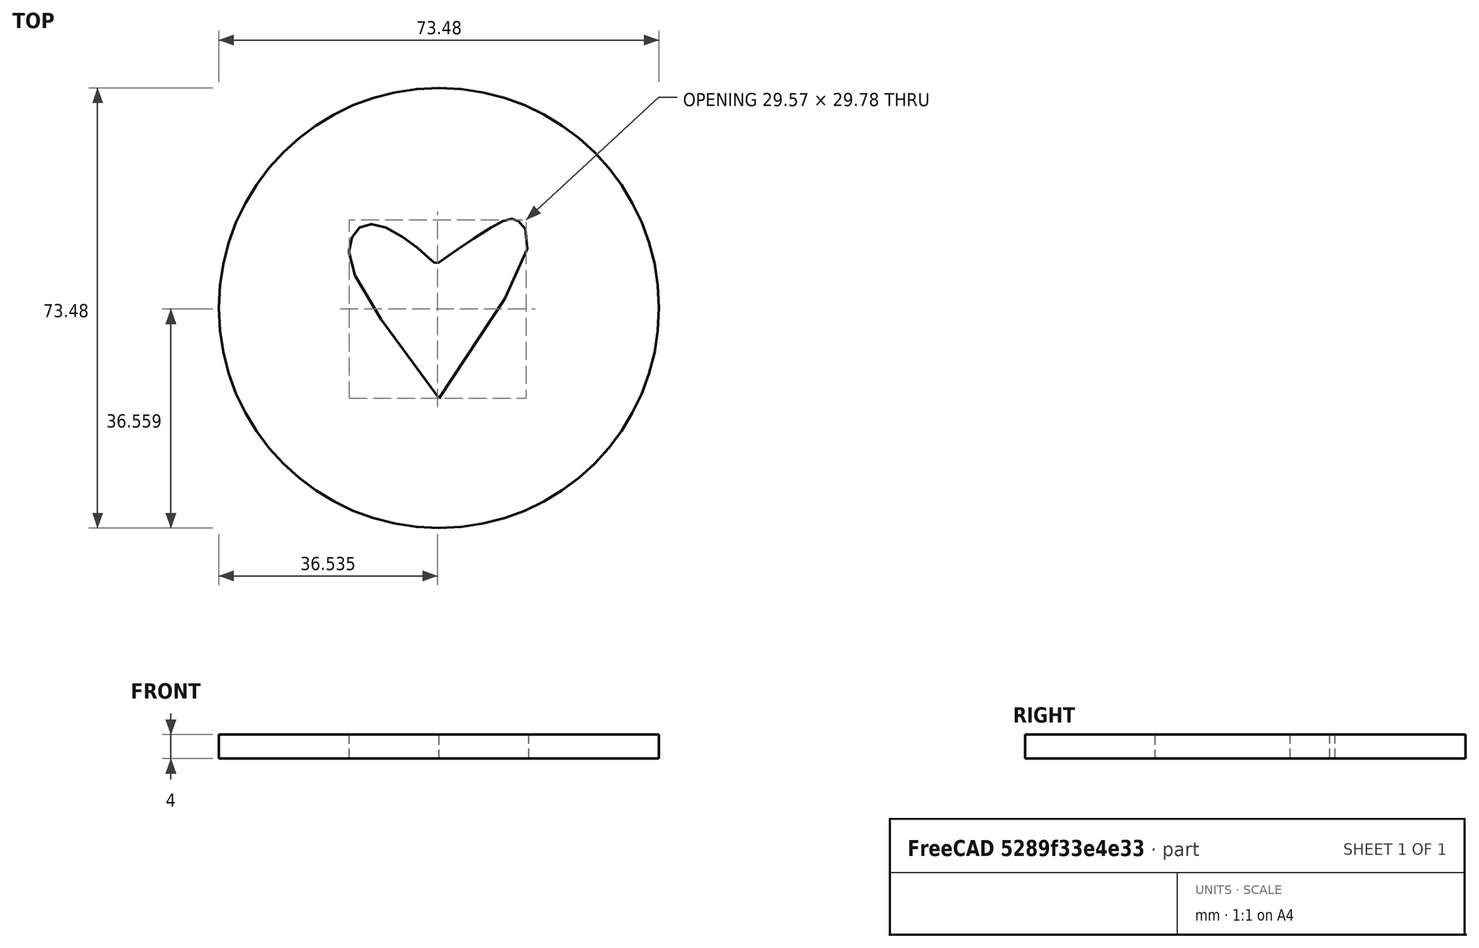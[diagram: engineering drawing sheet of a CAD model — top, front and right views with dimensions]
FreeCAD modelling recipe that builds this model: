
FCSTD DOCUMENT  (FreeCAD 1.0R38806 (Git))
Label: corazon
License: All rights reserved
LicenseURL: https://en.wikipedia.org/wiki/All_rights_reserved
objects: Sketcher::SketchObject×1, Part::Extrusion×1
note: 3 computed .brp shape members not serialized (recipe doc carries the construction recipe); baked Part::Feature solids carry a one-line shape summary decoded from their .brp

FEATURE [Sketcher::SketchObject] Sketch
  ArcFitTolerance = 1e-06
  FullyConstrained = false
  MakeInternals = false
  sketch-geometry (20):
    g0: Circle CenterX=0 CenterY=0 CenterZ=0 NormalX=0 NormalY=0 NormalZ=1 AngleXU=0 Radius=36.7446
    g1-g10: Circle [constr] x10 (B-spline internal-alignment scaffolding for g11; pole/knot coordinates omitted)
    g11: BSplineCurve PolesCount=10 KnotsCount=8 Degree=3 IsPeriodic=0
    g12-g19: GeomPoint [constr] x8 (B-spline internal-alignment scaffolding for g11; pole/knot coordinates omitted)
  constraints (9):
    c: Coincident(g0,g-1)
    c: Weight(g1) = 1
    c: Equal(g1, g2-g10) x9
    c: InternalAlignment(g1-g10 -> g11) x10
    c: InternalAlignment(g12-g19 -> g11) x8
    c: PointOnObject(g1,g-2)
    c: PointOnObject(g5,g-2)
    c: PointOnObject(g6,g5)
    c: Coincident(g10,g1)
FEATURE [Part::Extrusion] Extrude
  Base = -> Sketch
  Dir = (0,0,1)
  DirMode = 2
  FaceMakerClass = Part::FaceMakerBullseye
  FaceMakerMode = 3
  LengthFwd = 4
  LengthRev = 0
  Solid = true
  Symmetric = false
